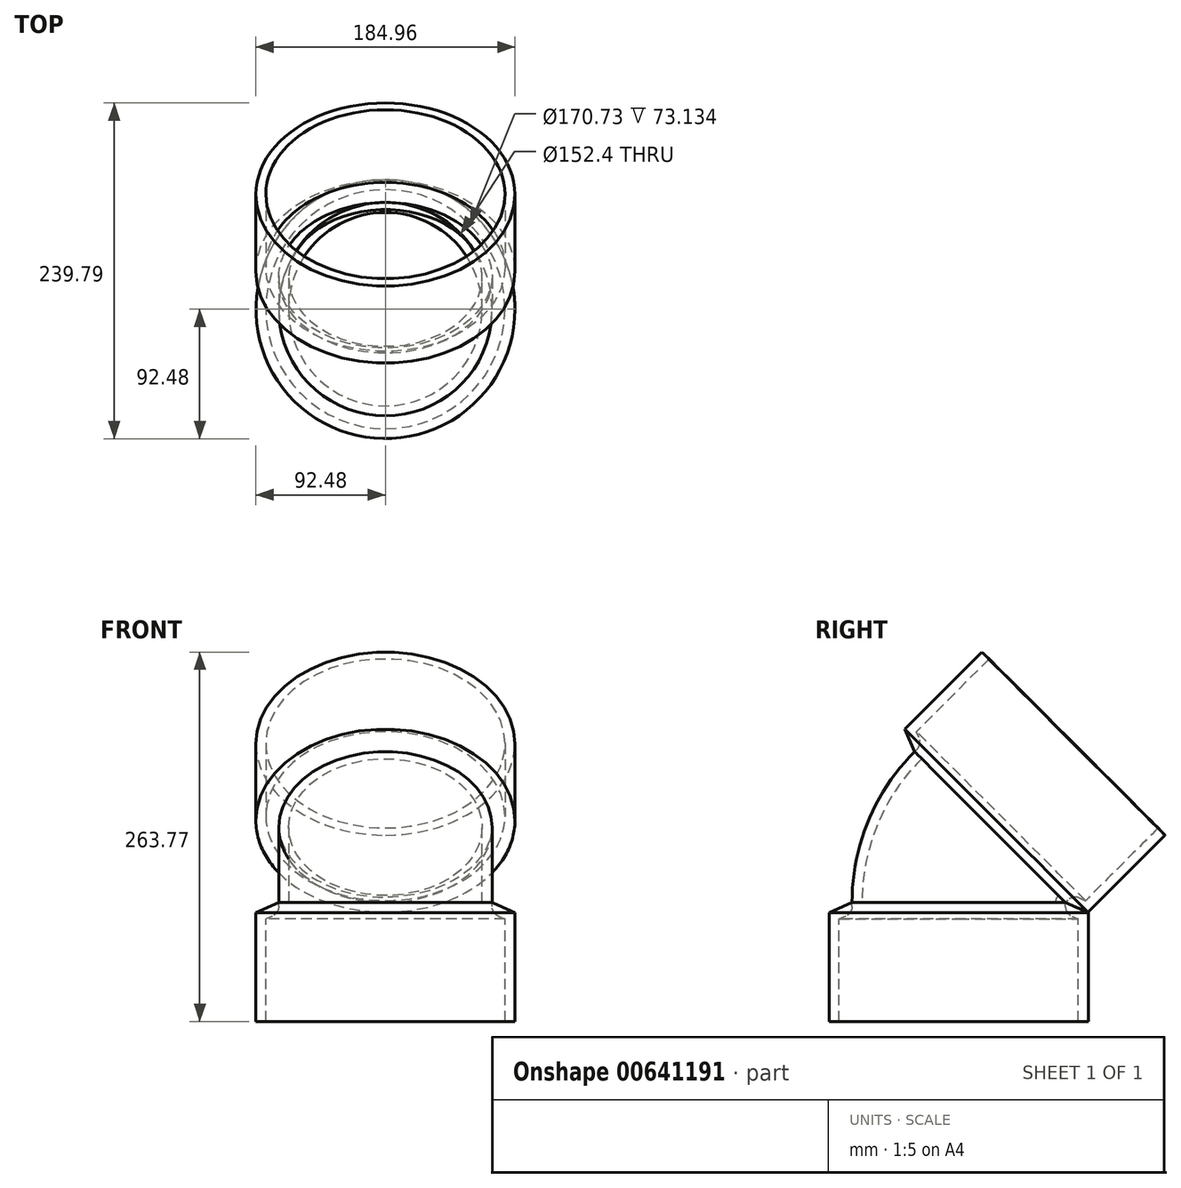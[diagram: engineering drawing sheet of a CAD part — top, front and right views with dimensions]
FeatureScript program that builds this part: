
annotation { "Feature Type Name" : "Feature", "Feature Type Description" : "" }
export const myFeature = defineFeature(function(context is Context, id is Id, definition is map)
    precondition{}
    {
        {
            var Q0;
            Q0=qCreatedBy(makeId("Right.planeOp"),FACE);
            var sketch = newSketch(context, id + "F0", { "sketchPlane" : qUnion([Q0])});
            skLineSegment(sketch, "E0", {"start": v(0, 0) * mm, "end": v(-76.2, 0) * mm});
            skLineSegment(sketch, "E1", {"start": v(0, 0) * mm, "end": v(0, -7.11) * mm});
            skLineSegment(sketch, "E2", {"start": v(0, -7.11) * mm, "end": v(0, -84.9) * mm});
            skLineSegment(sketch, "E3.0", {"start": v(-92.48, -7.11) * mm, "end": v(-92.48, -84.9) * mm});
            skLineSegment(sketch, "E4", {"start": v(-76.2, 0) * mm, "end": v(-92.48, -7.11) * mm});
            skLineSegment(sketch, "E5.0", {"start": v(-85.36, -11.77) * mm, "end": v(-85.36, -84.9) * mm});
            skLineSegment(sketch, "E5.1", {"start": v(-76.2, -7.76) * mm, "end": v(-85.36, -11.77) * mm});
            skLineSegment(sketch, "E6", {"start": v(-92.48, -84.9) * mm, "end": v(-85.36, -84.9) * mm});
            skLineSegment(sketch, "E7", {"start": v(-76.2, 0) * mm, "end": v(-76.2, -7.76) * mm});
            skSolve(sketch);
        }
        {
            var Q0;
            Q0=qCreatedBy(makeId("Top.planeOp"),FACE);
            var sketch = newSketch(context, id + "F1", { "sketchPlane" : qUnion([Q0])});
            skCircle(sketch, "E8", {"center": v(0, 0) * mm, "radius": 76.2 * mm});
            skCircle(sketch, "E9.0", {"center": v(0, 0) * mm, "radius": 69.09 * mm});
            skSolve(sketch);
        }
        {
            var Q0;
            Q0=qCreatedBy(makeId("Right.planeOp"),FACE);
            var sketch = newSketch(context, id + "F2", { "sketchPlane" : qUnion([Q0])});
            skArc(sketch, "E10", {"start": v(22.32, 53.88) * mm, "mid": v(5.8, 29.16) * mm, "end": v(0, 0) * mm});
            skSolve(sketch);
        }
        {
            var Q0;
            Q0=qCreatedBy(makeId("Right.planeOp"),FACE);
            var sketch = newSketch(context, id + "F3", { "sketchPlane" : qUnion([Q0])});
            skLineSegment(sketch, "E11", {"start": v(22.32, 53.88) * mm, "end": v(-31.56, 107.76) * mm});
            skLineSegment(sketch, "E12", {"start": v(22.32, 53.88) * mm, "end": v(27.35, 58.91) * mm});
            skLineSegment(sketch, "E13", {"start": v(27.35, 58.91) * mm, "end": v(82.35, 113.91) * mm});
            skLineSegment(sketch, "E14.0", {"start": v(-38.48, 123.86) * mm, "end": v(16.53, 178.87) * mm});
            skLineSegment(sketch, "E15", {"start": v(-38.48, 123.86) * mm, "end": v(-31.56, 107.76) * mm});
            skLineSegment(sketch, "E16.0", {"start": v(-30.17, 122.12) * mm, "end": v(21.73, 174.02) * mm});
            skLineSegment(sketch, "E17", {"start": v(-26.23, 112.94) * mm, "end": v(-30.17, 122.12) * mm});
            skLineSegment(sketch, "E18", {"start": v(-31.56, 107.76) * mm, "end": v(-26.27, 113.05) * mm});
            skLineSegment(sketch, "E19", {"start": v(16.53, 178.87) * mm, "end": v(21.73, 174.02) * mm});
            skLineSegment(sketch, "E20", {"start": v(22.32, 53.88) * mm, "end": v(107.45, 53.88) * mm});
            skSolve(sketch);
        }
        {
            var Q0;
            Q0=makeQuery(id+"F0.imprint","IMPRINT",FACE,{"disambiguationData":[TD([[makeQuery(id+"F0.imprint","IMPRINT",EDGE,{"derivedFrom":sQuery(id+"F0.wireOp",EDGE,"E3.0")}),1.0]])]});
            var Q1;
            Q1=sQuery(id+"F0.wireOp",EDGE,"E2");
            revolve(context, id + "F4", {"entities" : qUnion([Q0]), "axis" : qUnion([Q1]), "revolveType" : RevolveType.FULL});
        }
        {
            var Q0;
            Q0=makeQuery(id+"F1.imprint","IMPRINT",FACE,{"disambiguationData":[TD([[makeQuery(id+"F1.imprint","IMPRINT",EDGE,{"derivedFrom":sQuery(id+"F1.wireOp",EDGE,"E8")}),1.0]])]});
            var Q1;
            Q1=sQuery(id+"F2.wireOp",EDGE,"E10");
            sweep(context, id + "F5", {"operationType" : NewBodyOperationType.ADD, "profiles" : qUnion([Q0]), "path" : qUnion([Q1])});
        }
        {
            var Q0;
            Q0=makeQuery(id+"F3.imprint","IMPRINT",FACE,{"disambiguationData":[TD([[makeQuery(id+"F3.imprint","IMPRINT",EDGE,{"derivedFrom":sQuery(id+"F3.wireOp",EDGE,"E14.0")}),-1.0]])]});
            var Q1;
            Q1=sQuery(id+"F3.wireOp",EDGE,"E13");
            revolve(context, id + "F6", {"operationType" : NewBodyOperationType.ADD, "entities" : qUnion([Q0]), "axis" : qUnion([Q1]), "revolveType" : RevolveType.FULL});
        }
        {
            var Q0;
            Q0=makeQuery(id+"F6.opRevolve","SWEPT_EDGE",EDGE,{"disambiguationData":[OSD([sQuery(id+"F3.wireOp",EDGE,"E17"),sQuery(id+"F3.wireOp",EDGE,"E18")])]});
            fillet(context, id + "F7", {"entities" : qUnion([Q0]), "radius" : 7.62 * mm, "tangentPropagation" : true, "allowEdgeOverflow" : false});
        }
        {
            var Q0;
            Q0=makeQuery(id+"F4.opRevolve","SWEPT_EDGE",EDGE,{"disambiguationData":[OSD([sQuery(id+"F0.wireOp",EDGE,"E5.1"),sQuery(id+"F0.wireOp",EDGE,"E7")])]});
            fillet(context, id + "F8", {"entities" : qUnion([Q0]), "radius" : 7.62 * mm, "tangentPropagation" : true, "allowEdgeOverflow" : false});
        }
    });
